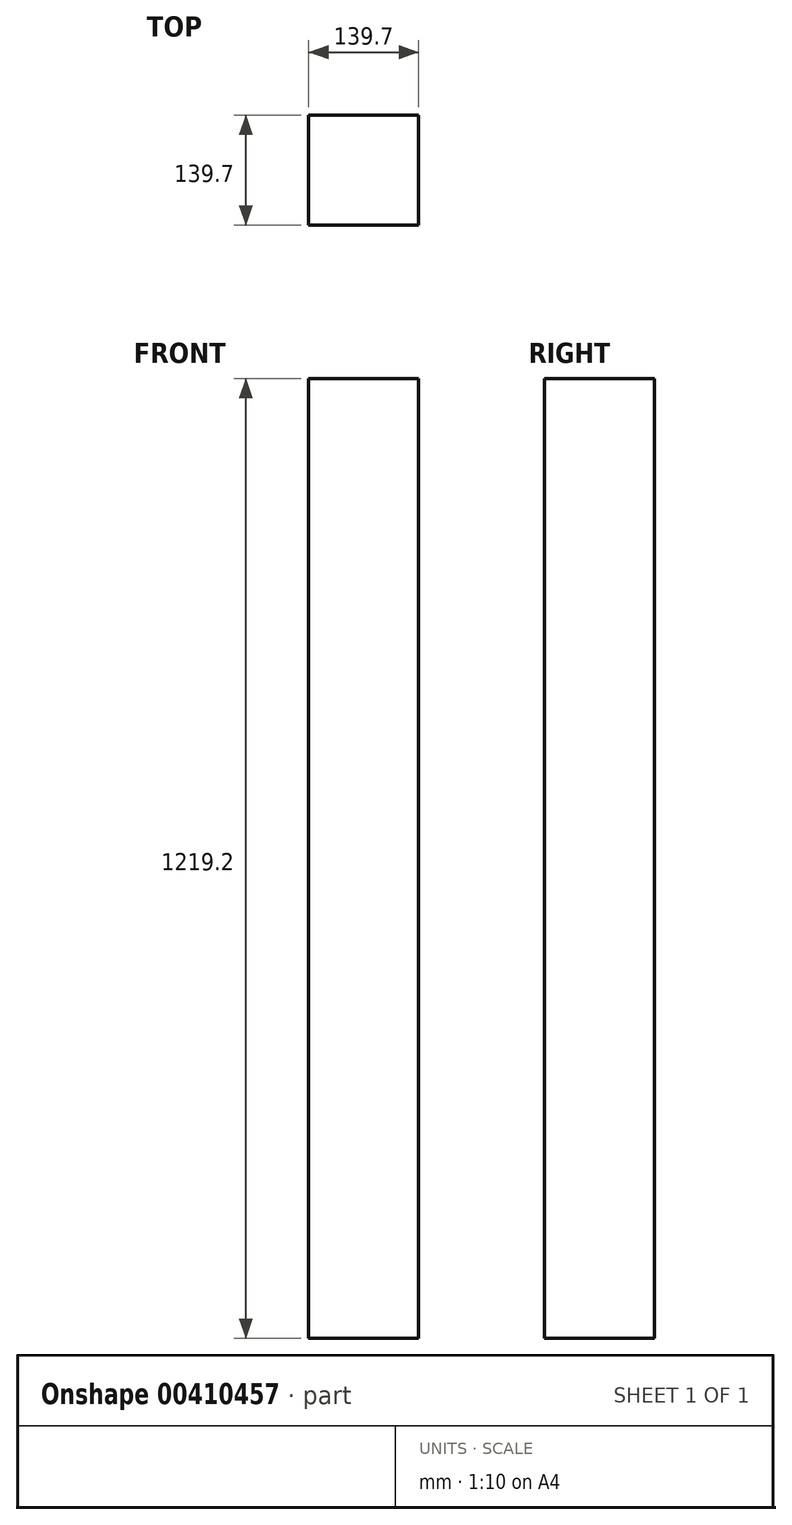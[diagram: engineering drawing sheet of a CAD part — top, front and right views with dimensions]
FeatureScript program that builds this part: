
annotation { "Feature Type Name" : "Feature", "Feature Type Description" : "" }
export const myFeature = defineFeature(function(context is Context, id is Id, definition is map)
    precondition{}
    {
        {
            var Q0;
            Q0=qCreatedBy(makeId("Front.planeOp"),FACE);
            var sketch = newSketch(context, id + "F0", { "sketchPlane" : qUnion([Q0])});
            skLineSegment(sketch, "E0.bottom", {"start": v(-69.85, 609.6) * mm, "end": v(69.85, 609.6) * mm});
            skLineSegment(sketch, "E0.top", {"start": v(-69.85, -609.6) * mm, "end": v(69.85, -609.6) * mm});
            skLineSegment(sketch, "E0.left", {"start": v(-69.85, 609.6) * mm, "end": v(-69.85, -609.6) * mm});
            skLineSegment(sketch, "E0.right", {"start": v(69.85, 609.6) * mm, "end": v(69.85, -609.6) * mm});
            skPoint(sketch, "E0.middle", {"position": v(0, 0) * mm});
            skSolve(sketch);
        }
        {
            var Q0;
            Q0=qSketchRegion(id+"F0",true);
            extrude(context, id + "F1", {"entities" : qUnion([Q0]), "depth" : 139.7 * mm, "offsetDistance" : 25.4 * mm, "symmetric" : true});
        }
    });
